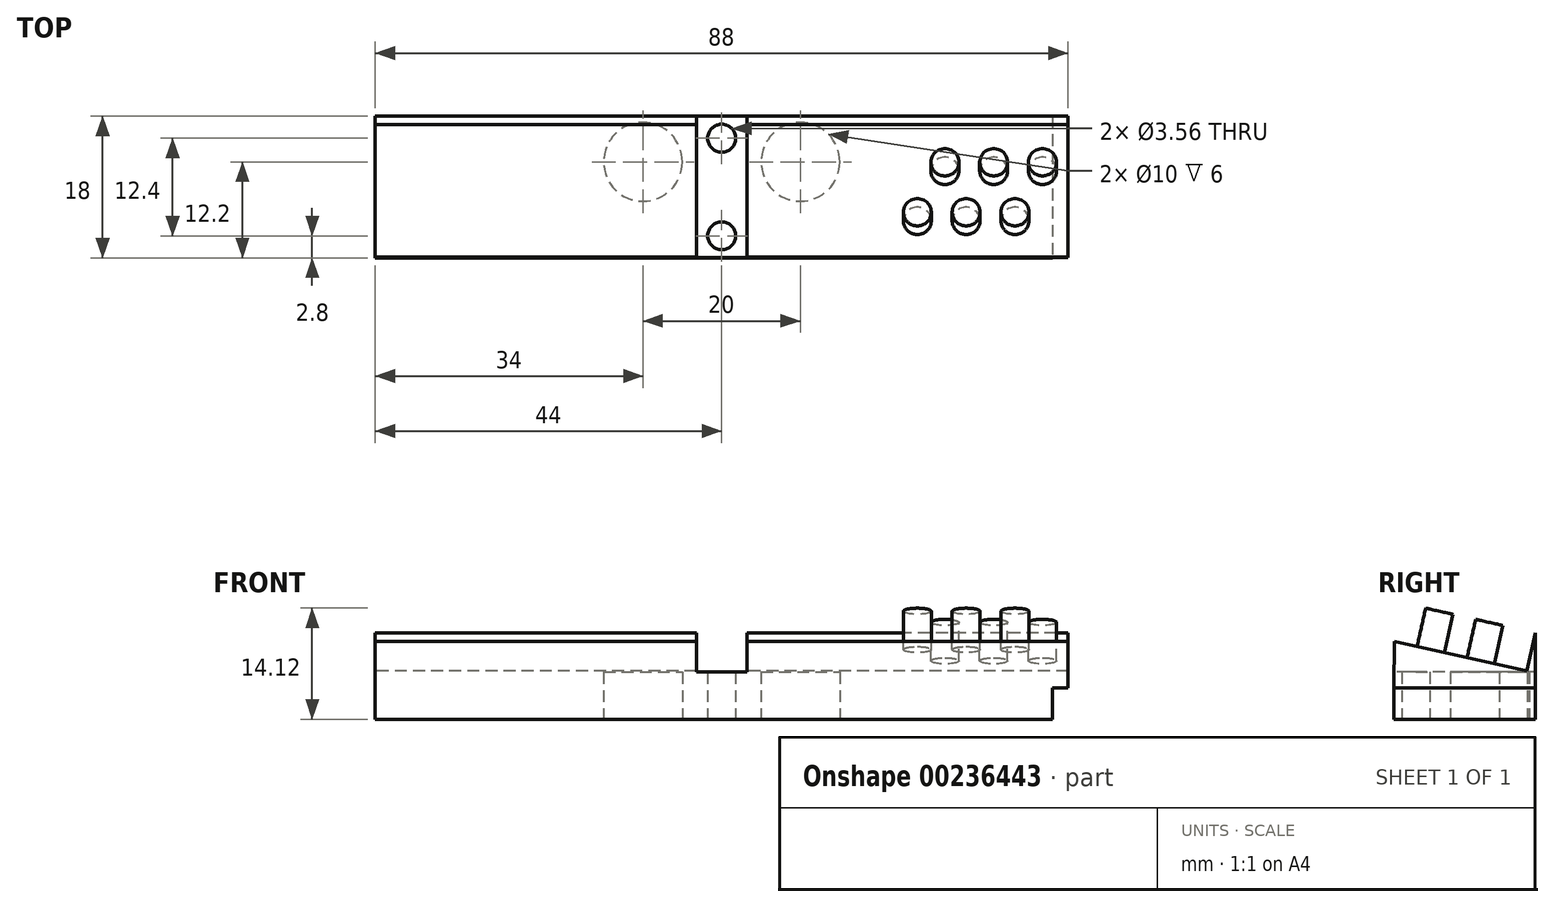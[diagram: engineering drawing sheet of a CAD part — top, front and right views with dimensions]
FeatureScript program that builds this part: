
annotation { "Feature Type Name" : "Feature", "Feature Type Description" : "" }
export const myFeature = defineFeature(function(context is Context, id is Id, definition is map)
    precondition{}
    {
        {
            var Q0;
            Q0=qCreatedBy(makeId("Right.planeOp"),FACE);
            var sketch = newSketch(context, id + "F0", { "sketchPlane" : qUnion([Q0])});
            skLineSegment(sketch, "E0", {"start": v(0, 0) * mm, "end": v(0.15, 15) * mm});
            skLineSegment(sketch, "E1", {"start": v(0.15, 15) * mm, "end": v(18, 11) * mm});
            skLineSegment(sketch, "E2", {"start": v(18, 11) * mm, "end": v(18, 0) * mm});
            skLineSegment(sketch, "E3", {"start": v(18, 0) * mm, "end": v(0, 0) * mm});
            skSolve(sketch);
        }
        {
            var Q0;
            Q0 = qSketchRegion(id + "F0", true);
            extrude(context, id + "F1", {"entities" : qUnion([Q0]), "depth" : 88 * mm});
        }
        {
            var Q0;
            Q0=makeQuery(id+"F1.opExtrude","SWEPT_FACE",FACE,{"disambiguationData":[OSD([sQuery(id+"F0.wireOp",EDGE,"E1")])]});
            var sketch = newSketch(context, id + "F2", { "sketchPlane" : qUnion([Q0])});
            skCircle(sketch, "E4", {"center": v(3.25, 9.16) * mm, "radius": 1.78 * mm});
            skCircle(sketch, "E5.1.0.0", {"center": v(9.45, 9.16) * mm, "radius": 1.78 * mm});
            skCircle(sketch, "E5.2.0.0", {"center": v(15.65, 9.16) * mm, "radius": 1.78 * mm});
            skLineSegment(sketch, "E5.direction1", {"start": v(3.25, 9.16) * mm, "end": v(9.45, 9.16) * mm, "construction": true});
            skCircle(sketch, "E6", {"center": v(6.75, 2.66) * mm, "radius": 1.78 * mm});
            skCircle(sketch, "E7.1.0.0", {"center": v(12.95, 2.66) * mm, "radius": 1.78 * mm});
            skCircle(sketch, "E7.2.0.0", {"center": v(19.15, 2.66) * mm, "radius": 1.78 * mm});
            skLineSegment(sketch, "E7.direction1", {"start": v(6.75, 2.66) * mm, "end": v(12.95, 2.66) * mm, "construction": true});
            skLineSegment(sketch, "E8", {"start": v(44, 15.16) * mm, "end": v(44, -3.13) * mm, "construction": true});
            skCircle(sketch, "E9.MirrorC", {"center": v(75.05, 2.66) * mm, "radius": 1.78 * mm});
            skLineSegment(sketch, "E10.MirrorCS", {"start": v(81.25, 2.66) * mm, "end": v(75.05, 2.66) * mm, "construction": true});
            skCircle(sketch, "E11.MirrorC", {"center": v(68.85, 2.66) * mm, "radius": 1.78 * mm});
            skCircle(sketch, "E12.MirrorC", {"center": v(81.25, 2.66) * mm, "radius": 1.78 * mm});
            skLineSegment(sketch, "E13.MirrorCS", {"start": v(84.75, 9.16) * mm, "end": v(78.55, 9.16) * mm, "construction": true});
            skCircle(sketch, "E14.MirrorC", {"center": v(72.35, 9.16) * mm, "radius": 1.78 * mm});
            skCircle(sketch, "E15.MirrorC", {"center": v(78.55, 9.16) * mm, "radius": 1.78 * mm});
            skCircle(sketch, "E16.MirrorC", {"center": v(84.75, 9.16) * mm, "radius": 1.78 * mm});
            skSolve(sketch);
        }
        {
            var Q0;
            Q0=makeQuery(id+"F2.imprint","IMPRINT",FACE,{"disambiguationData":[TD([[makeQuery(id+"F2.imprint","IMPRINT",EDGE,{"derivedFrom":sQuery(id+"F2.wireOp",EDGE,"E7.2.0.0")}),1.0]])]});
            var Q1;
            Q1=makeQuery(id+"F2.imprint","IMPRINT",FACE,{"disambiguationData":[TD([[makeQuery(id+"F2.imprint","IMPRINT",EDGE,{"derivedFrom":sQuery(id+"F2.wireOp",EDGE,"E7.1.0.0")}),1.0]])]});
            var Q2;
            Q2=makeQuery(id+"F2.imprint","IMPRINT",FACE,{"disambiguationData":[TD([[makeQuery(id+"F2.imprint","IMPRINT",EDGE,{"derivedFrom":sQuery(id+"F2.wireOp",EDGE,"E6")}),1.0]])]});
            var Q3;
            Q3=makeQuery(id+"F2.imprint","IMPRINT",FACE,{"disambiguationData":[TD([[makeQuery(id+"F2.imprint","IMPRINT",EDGE,{"derivedFrom":sQuery(id+"F2.wireOp",EDGE,"E5.2.0.0")}),1.0]])]});
            var Q4;
            Q4=makeQuery(id+"F2.imprint","IMPRINT",FACE,{"disambiguationData":[TD([[makeQuery(id+"F2.imprint","IMPRINT",EDGE,{"derivedFrom":sQuery(id+"F2.wireOp",EDGE,"E4")}),1.0]])]});
            var Q5;
            Q5=makeQuery(id+"F2.imprint","IMPRINT",FACE,{"disambiguationData":[TD([[makeQuery(id+"F2.imprint","IMPRINT",EDGE,{"derivedFrom":sQuery(id+"F2.wireOp",EDGE,"E9.MirrorC")}),-1.0]])]});
            var Q6;
            Q6=makeQuery(id+"F2.imprint","IMPRINT",FACE,{"disambiguationData":[TD([[makeQuery(id+"F2.imprint","IMPRINT",EDGE,{"derivedFrom":sQuery(id+"F2.wireOp",EDGE,"E11.MirrorC")}),-1.0]])]});
            var Q7;
            Q7=makeQuery(id+"F2.imprint","IMPRINT",FACE,{"disambiguationData":[TD([[makeQuery(id+"F2.imprint","IMPRINT",EDGE,{"derivedFrom":sQuery(id+"F2.wireOp",EDGE,"E12.MirrorC")}),-1.0]])]});
            var Q8;
            Q8=makeQuery(id+"F2.imprint","IMPRINT",FACE,{"disambiguationData":[TD([[makeQuery(id+"F2.imprint","IMPRINT",EDGE,{"derivedFrom":sQuery(id+"F2.wireOp",EDGE,"E14.MirrorC")}),-1.0]])]});
            var Q9;
            Q9=makeQuery(id+"F2.imprint","IMPRINT",FACE,{"disambiguationData":[TD([[makeQuery(id+"F2.imprint","IMPRINT",EDGE,{"derivedFrom":sQuery(id+"F2.wireOp",EDGE,"E15.MirrorC")}),-1.0]])]});
            var Q10;
            Q10=makeQuery(id+"F2.imprint","IMPRINT",FACE,{"disambiguationData":[TD([[makeQuery(id+"F2.imprint","IMPRINT",EDGE,{"derivedFrom":sQuery(id+"F2.wireOp",EDGE,"E16.MirrorC")}),-1.0]])]});
            var Q11;
            Q11=makeQuery(id+"F2.imprint","IMPRINT",FACE,{"disambiguationData":[TD([[makeQuery(id+"F2.imprint","IMPRINT",EDGE,{"derivedFrom":sQuery(id+"F2.wireOp",EDGE,"E5.1.0.0")}),1.0]])]});
            extrude(context, id + "F3", {"entities" : qUnion([Q0, Q1, Q2, Q3, Q4, Q5, Q6, Q7, Q8, Q9, Q10, Q11]), "operationType" : NewBodyOperationType.REMOVE, "oppositeDirection" : true, "depth" : 5 * mm});
        }
        {
            var Q0;
            Q0=makeQuery(id+"F1.opExtrude","SWEPT_FACE",FACE,{"disambiguationData":[OSD([sQuery(id+"F0.wireOp",EDGE,"E3")])]});
            var sketch = newSketch(context, id + "F4", { "sketchPlane" : qUnion([Q0])});
            skCircle(sketch, "E17", {"center": v(44, -15.2) * mm, "radius": 1.78 * mm});
            skPoint(sketch, "E17.centerSnap0", {"position": v(44, 0) * mm});
            skCircle(sketch, "E18.0.1.0", {"center": v(44, -2.8) * mm, "radius": 1.78 * mm});
            skLineSegment(sketch, "E18.direction1", {"start": v(44, -15.2) * mm, "end": v(69, -15.2) * mm, "construction": true});
            skLineSegment(sketch, "E18.direction2", {"start": v(44, -15.2) * mm, "end": v(44, -2.8) * mm, "construction": true});
            skSolve(sketch);
        }
        {
            var Q0;
            Q0 = qSketchRegion(id + "F4", true);
            extrude(context, id + "F5", {"entities" : qUnion([Q0]), "operationType" : NewBodyOperationType.REMOVE, "endBound" : BoundingType.UP_TO_NEXT, "oppositeDirection" : true, "depth" : 5 * mm});
        }
        {
            var Q0;
            Q0=qCreatedBy(makeId("Top.planeOp"),FACE);
            cPlane(context, id + "F6", {"entities" : qUnion([Q0]), "cplaneType" : CPlaneType.OFFSET, "offset" : 6 * mm, "width" : 150 * mm, "height" : 150 * mm});
        }
        {
            var Q0;
            Q0=qCreatedBy(id+"F6.planeOp",FACE);
            var sketch = newSketch(context, id + "F7", { "sketchPlane" : qUnion([Q0])});
            skLineSegment(sketch, "E19.bottom", {"start": v(40.8, 18.66) * mm, "end": v(47.2, 18.66) * mm});
            skLineSegment(sketch, "E19.top", {"start": v(40.8, -3.26) * mm, "end": v(47.2, -3.26) * mm});
            skLineSegment(sketch, "E19.left", {"start": v(40.8, 18.66) * mm, "end": v(40.8, -3.26) * mm});
            skLineSegment(sketch, "E19.right", {"start": v(47.2, 18.66) * mm, "end": v(47.2, -3.26) * mm});
            skSolve(sketch);
        }
        {
            var Q0;
            Q0 = qSketchRegion(id + "F7", true);
            extrude(context, id + "F8", {"entities" : qUnion([Q0]), "operationType" : NewBodyOperationType.REMOVE, "depth" : 25 * mm});
        }
        {
            var Q0;
            Q0=makeQuery(id+"F1.opExtrude","SWEPT_FACE",FACE,{"disambiguationData":[OSD([sQuery(id+"F0.wireOp",EDGE,"E3")])]});
            var sketch = newSketch(context, id + "F9", { "sketchPlane" : qUnion([Q0])});
            skCircle(sketch, "E20", {"center": v(54, -12.2) * mm, "radius": 5 * mm});
            skLineSegment(sketch, "E21", {"start": v(44, 0) * mm, "end": v(44, -18) * mm, "construction": true});
            skPoint(sketch, "E22", {"position": v(44, -15.2) * mm});
            skCircle(sketch, "E23.MirrorC", {"center": v(34, -12.2) * mm, "radius": 5 * mm});
            skSolve(sketch);
        }
        {
            var Q0;
            Q0 = qSketchRegion(id + "F9", true);
            extrude(context, id + "F10", {"entities" : qUnion([Q0]), "operationType" : NewBodyOperationType.REMOVE, "oppositeDirection" : true, "depth" : 6 * mm});
        }
        {
            var Q0;
            Q0=makeQuery(id+"F1.opExtrude","SWEPT_FACE",FACE,{"disambiguationData":[OSD([sQuery(id+"F0.wireOp",EDGE,"E3")])]});
            var sketch = newSketch(context, id + "F11", { "sketchPlane" : qUnion([Q0])});
            skLineSegment(sketch, "E24.bottom", {"start": v(88, -18) * mm, "end": v(86, -18) * mm});
            skLineSegment(sketch, "E24.top", {"start": v(88, 0) * mm, "end": v(86, 0) * mm});
            skLineSegment(sketch, "E24.left", {"start": v(88, -18) * mm, "end": v(88, 0) * mm});
            skLineSegment(sketch, "E24.right", {"start": v(86, -18) * mm, "end": v(86, 0) * mm});
            skSolve(sketch);
        }
        {
            var Q0;
            Q0 = qSketchRegion(id + "F11", true);
            extrude(context, id + "F12", {"entities" : qUnion([Q0]), "operationType" : NewBodyOperationType.REMOVE, "oppositeDirection" : true, "depth" : 4 * mm});
        }
    });
